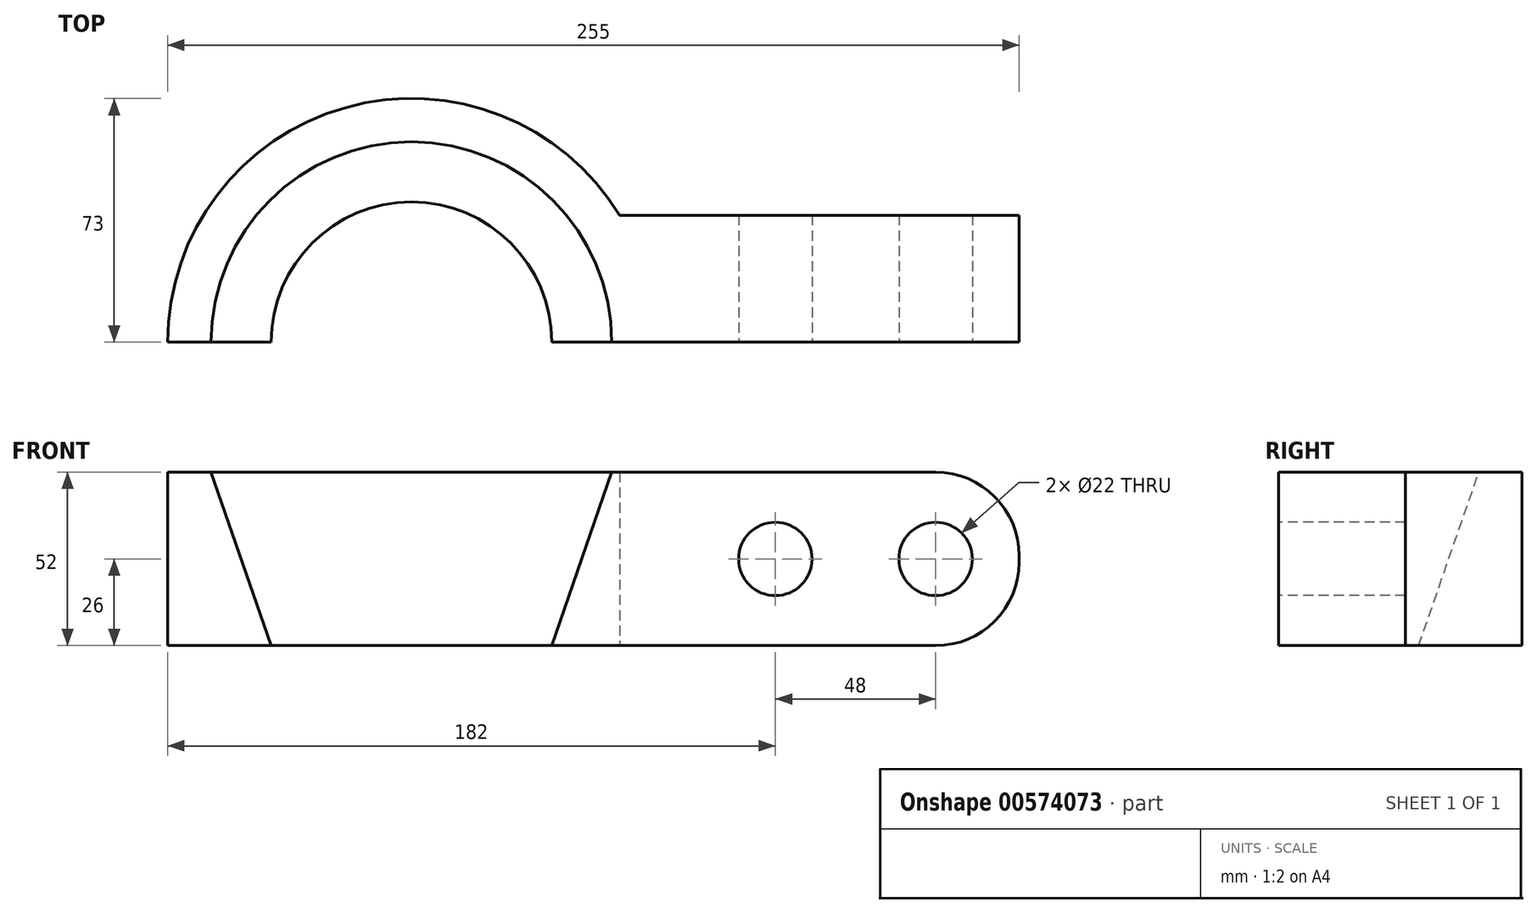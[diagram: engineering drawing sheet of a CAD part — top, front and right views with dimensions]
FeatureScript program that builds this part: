
annotation { "Feature Type Name" : "Feature", "Feature Type Description" : "" }
export const myFeature = defineFeature(function(context is Context, id is Id, definition is map)
    precondition{}
    {
        {
            var Q0;
            Q0=qCreatedBy(makeId("Top.planeOp"),FACE);
            var sketch = newSketch(context, id + "F0", { "sketchPlane" : qUnion([Q0])});
            skArc(sketch, "E0", {"start": v(62.33, 38) * mm, "mid": v(-19.73, 70.28) * mm, "end": v(-73, 0) * mm});
            skLineSegment(sketch, "E1", {"start": v(62.33, 38) * mm, "end": v(182, 38) * mm});
            skLineSegment(sketch, "E2", {"start": v(182, 38) * mm, "end": v(182, 0) * mm});
            skLineSegment(sketch, "E3", {"start": v(182, 0) * mm, "end": v(-73, 0) * mm});
            skPoint(sketch, "E4.orphan", {"position": v(0, 38) * mm});
            skSolve(sketch);
        }
        {
            var Q0;
            Q0 = qSketchRegion(id + "F0", true);
            extrude(context, id + "F1", {"entities" : qUnion([Q0]), "depth" : 52 * mm, "offsetDistance" : 25 * mm});
        }
        {
            var Q0;
            Q0=makeQuery(id+"F1.opExtrude","SWEPT_FACE",FACE,{"disambiguationData":[OSD([sQuery(id+"F0.wireOp",EDGE,"E3")])]});
            var sketch = newSketch(context, id + "F2", { "sketchPlane" : qUnion([Q0])});
            skCircle(sketch, "E5", {"center": v(109, 26) * mm, "radius": 11 * mm});
            skCircle(sketch, "E6", {"center": v(157, 26) * mm, "radius": 11 * mm});
            skSolve(sketch);
        }
        {
            var Q0;
            Q0=makeQuery(id+"F2.imprint","IMPRINT",FACE,{"disambiguationData":[TD([[makeQuery(id+"F2.imprint","IMPRINT",EDGE,{"derivedFrom":sQuery(id+"F2.wireOp",EDGE,"E5")}),1.0]])]});
            var Q1;
            Q1=makeQuery(id+"F2.imprint","IMPRINT",FACE,{"disambiguationData":[TD([[makeQuery(id+"F2.imprint","IMPRINT",EDGE,{"derivedFrom":sQuery(id+"F2.wireOp",EDGE,"E6")}),1.0]])]});
            extrude(context, id + "F3", {"entities" : qUnion([Q0, Q1]), "operationType" : NewBodyOperationType.REMOVE, "oppositeDirection" : true, "depth" : 38 * mm, "offsetDistance" : 25 * mm});
        }
        {
            var Q0;
            Q0=makeQuery(id+"F1.opExtrude","SWEPT_FACE",FACE,{"disambiguationData":[OSD([sQuery(id+"F0.wireOp",EDGE,"E3")])]});
            var sketch = newSketch(context, id + "F4", { "sketchPlane" : qUnion([Q0])});
            skLineSegment(sketch, "E7", {"start": v(0, 52) * mm, "end": v(-60, 52) * mm});
            skLineSegment(sketch, "E8", {"start": v(-60, 52) * mm, "end": v(-42, 0) * mm});
            skLineSegment(sketch, "E9", {"start": v(-42, 0) * mm, "end": v(0, 0) * mm});
            skLineSegment(sketch, "E10", {"start": v(0, 0) * mm, "end": v(0, 52) * mm});
            skSolve(sketch);
        }
        {
            var Q0;
            Q0=makeQuery(id+"F4.imprint","IMPRINT",FACE,{"disambiguationData":[TD([[makeQuery(id+"F4.imprint","IMPRINT",EDGE,{"derivedFrom":sQuery(id+"F4.wireOp",EDGE,"E7")}),1.0]])]});
            var Q1;
            Q1=sQuery(id+"F4.wireOp",EDGE,"E10");
            revolve(context, id + "F5", {"operationType" : NewBodyOperationType.REMOVE, "entities" : qUnion([Q0]), "axis" : qUnion([Q1]), "revolveType" : RevolveType.FULL, "oppositeDirection" : true});
        }
        {
            var Q0;
            Q0=makeQuery(id+"F1.opExtrude","CAP_EDGE",EDGE,{"disambiguationData":[OSD([sQuery(id+"F0.wireOp",EDGE,"E2")])],"isStart":false});
            var Q1;
            Q1=makeQuery(id+"F1.opExtrude","CAP_EDGE",EDGE,{"disambiguationData":[OSD([sQuery(id+"F0.wireOp",EDGE,"E2")])],"isStart":true});
            fillet(context, id + "F6", {"entities" : qUnion([Q0, Q1]), "radius" : 25 * mm, "tangentPropagation" : true, "allowEdgeOverflow" : false});
        }
    });
